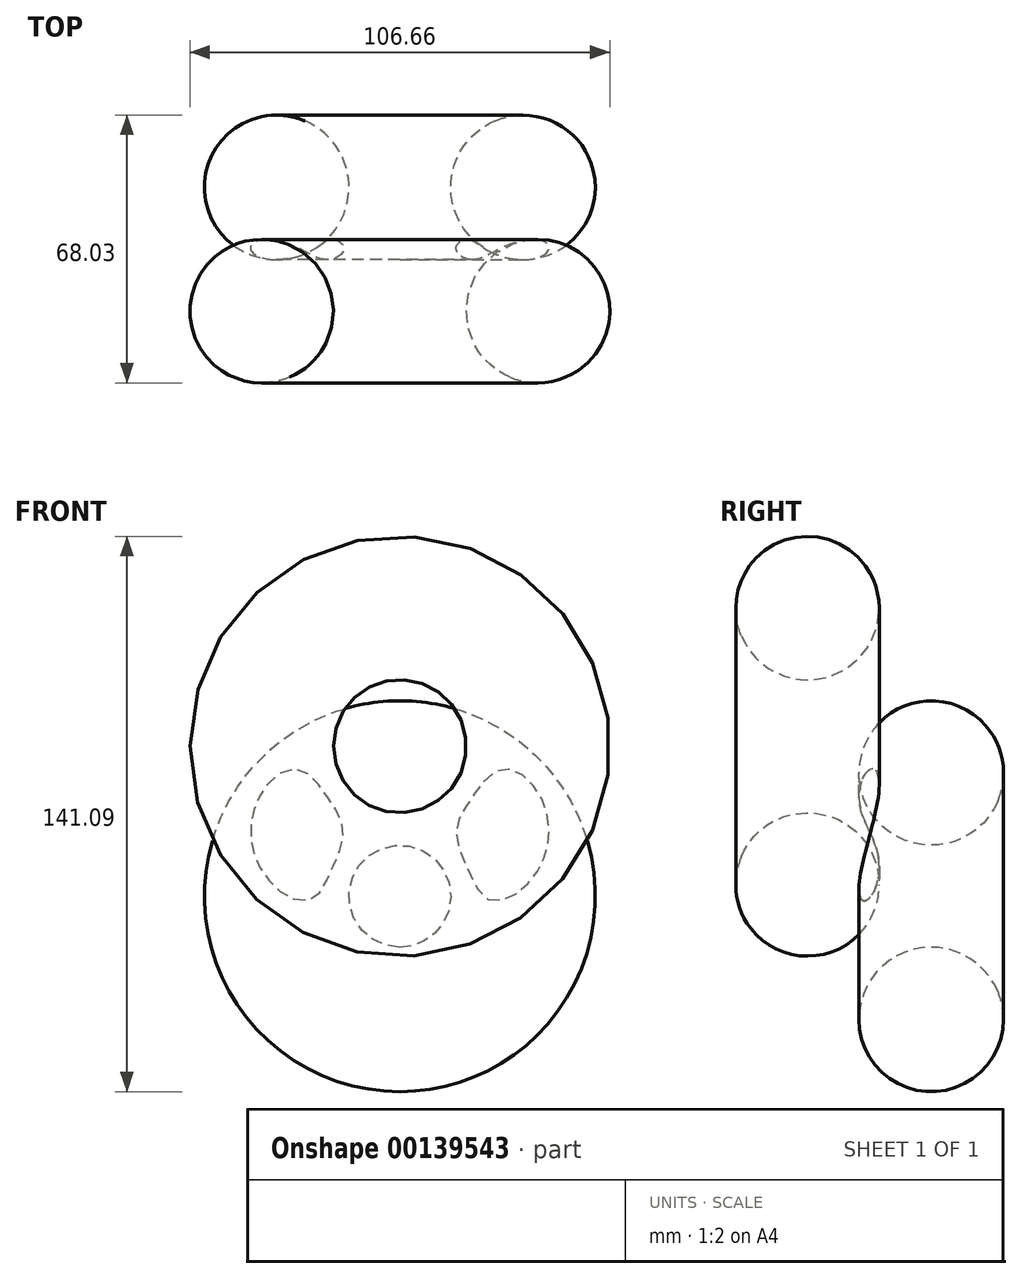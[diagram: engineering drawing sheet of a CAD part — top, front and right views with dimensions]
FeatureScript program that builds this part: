
annotation { "Feature Type Name" : "Feature", "Feature Type Description" : "" }
export const myFeature = defineFeature(function(context is Context, id is Id, definition is map)
    precondition{}
    {
        {
            var Q0;
            Q0=qCreatedBy(makeId("Top.planeOp"),FACE);
            var sketch = newSketch(context, id + "F0", { "sketchPlane" : qUnion([Q0])});
            skCircle(sketch, "E0", {"center": v(31.3, 0) * mm, "radius": 18.36 * mm});
            skLineSegment(sketch, "E1", {"start": v(0, 43.15) * mm, "end": v(0, -39.64) * mm});
            skSolve(sketch);
        }
        {
            var Q0;
            Q0=makeQuery(id+"F0.imprint","IMPRINT",FACE,{"disambiguationData":[TD([[makeQuery(id+"F0.imprint","IMPRINT",EDGE,{"derivedFrom":sQuery(id+"F0.wireOp",EDGE,"E0")}),1.0]])]});
            var Q1;
            Q1=sQuery(id+"F0.wireOp",EDGE,"E1");
            revolve(context, id + "F1", {"entities" : qUnion([Q0]), "axis" : qUnion([Q1]), "revolveType" : RevolveType.FULL});
        }
        {
            var Q0;
            Q0=qCreatedBy(makeId("Top.planeOp"),FACE);
            cPlane(context, id + "F2", {"entities" : qUnion([Q0]), "cplaneType" : CPlaneType.OFFSET, "offset" : 38.1 * mm, "width" : 152.4 * mm, "height" : 152.4 * mm});
        }
        {
            var Q0;
            Q0=qCreatedBy(id+"F2.planeOp",FACE);
            var sketch = newSketch(context, id + "F3", { "sketchPlane" : qUnion([Q0])});
            skCircle(sketch, "E2", {"center": v(35.1, -31.45) * mm, "radius": 18.22 * mm});
            skLineSegment(sketch, "E3", {"start": v(0, 56.02) * mm, "end": v(0, -46.37) * mm});
            skSolve(sketch);
        }
        {
            var Q0;
            Q0=makeQuery(id+"F3.imprint","IMPRINT",FACE,{"disambiguationData":[TD([[makeQuery(id+"F3.imprint","IMPRINT",EDGE,{"derivedFrom":sQuery(id+"F3.wireOp",EDGE,"E2")}),1.0]])]});
            var Q1;
            Q1=sQuery(id+"F3.wireOp",EDGE,"E3");
            revolve(context, id + "F4", {"operationType" : NewBodyOperationType.ADD, "entities" : qUnion([Q0]), "axis" : qUnion([Q1]), "revolveType" : RevolveType.FULL});
        }
    });
